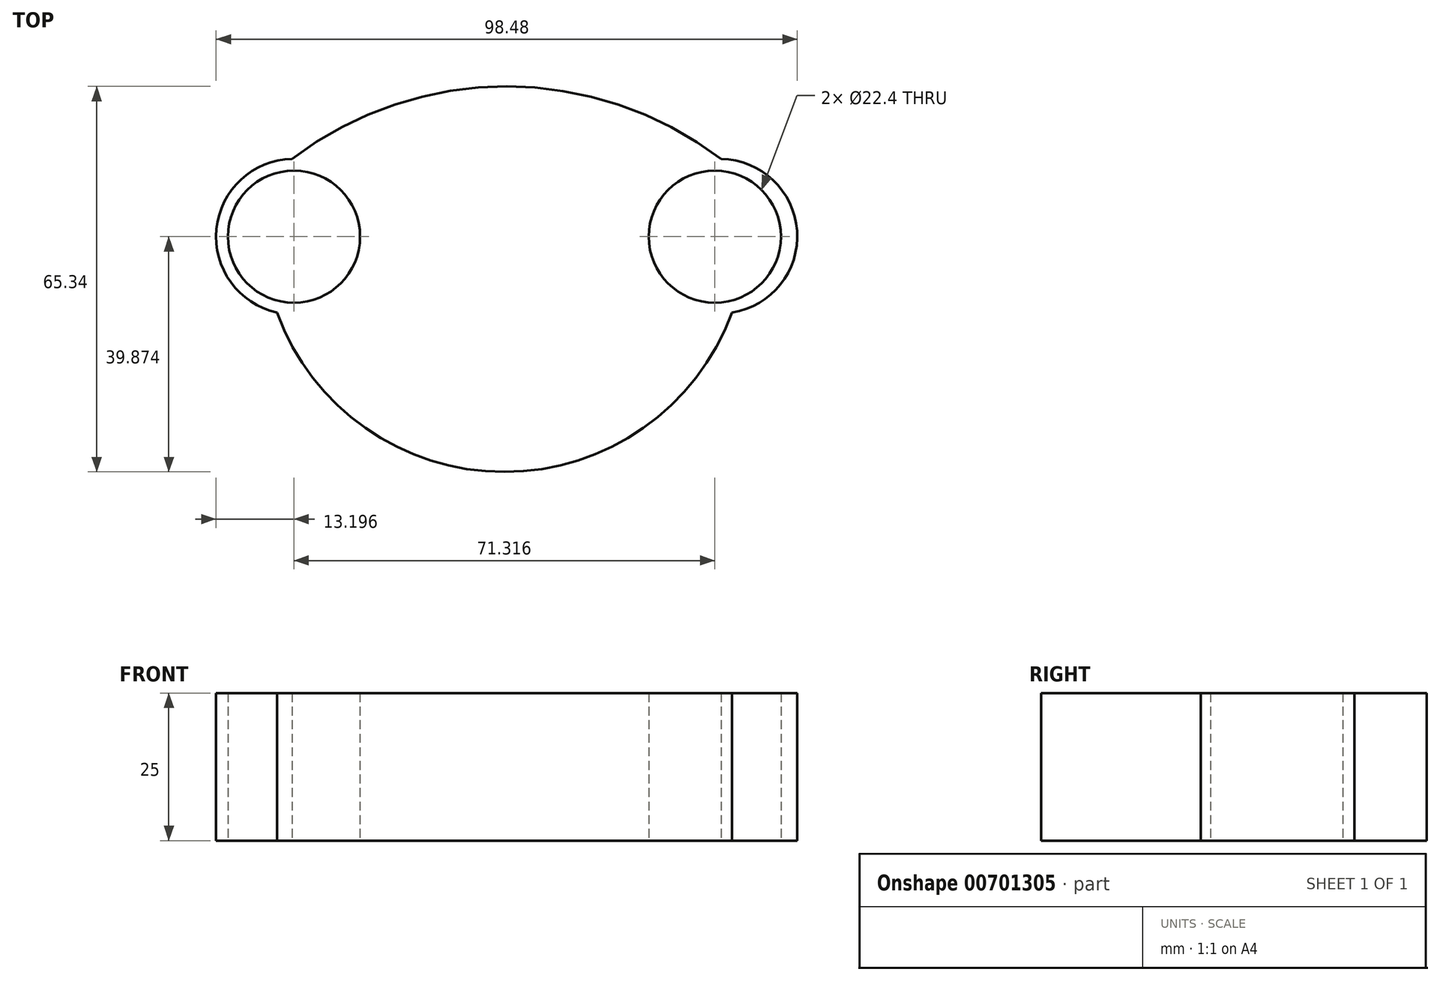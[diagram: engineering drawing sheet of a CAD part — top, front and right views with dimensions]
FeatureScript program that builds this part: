
annotation { "Feature Type Name" : "Feature", "Feature Type Description" : "" }
export const myFeature = defineFeature(function(context is Context, id is Id, definition is map)
    precondition{}
    {
        {
            var Q0;
            Q0=qCreatedBy(makeId("Top.planeOp"),FACE);
            var sketch = newSketch(context, id + "F0", { "sketchPlane" : qUnion([Q0])});
            skCircle(sketch, "E0", {"center": v(-36.48, 25.2) * mm, "radius": 11.2 * mm});
            skArc(sketch, "E1", {"start": v(-36.8, 38.4) * mm, "mid": v(-49.62, 26.5) * mm, "end": v(-39.38, 12.32) * mm});
            skCircle(sketch, "E2", {"center": v(34.83, 25.2) * mm, "radius": 11.2 * mm});
            skArc(sketch, "E3", {"start": v(35.89, 38.35) * mm, "mid": v(-0.45, 50.66) * mm, "end": v(-36.8, 38.4) * mm});
            skArc(sketch, "E4", {"start": v(-39.38, 12.32) * mm, "mid": v(-0.83, -14.68) * mm, "end": v(37.72, 12.32) * mm});
            skArc(sketch, "E5", {"start": v(37.72, 12.32) * mm, "mid": v(48.77, 26.18) * mm, "end": v(35.89, 38.35) * mm});
            skSolve(sketch);
        }
        {
            var Q0;
            Q0 = qSketchRegion(id + "F0", true);
            extrude(context, id + "F1", {"entities" : qUnion([Q0]), "depth" : 25 * mm, "offsetDistance" : 25 * mm});
        }
    });
